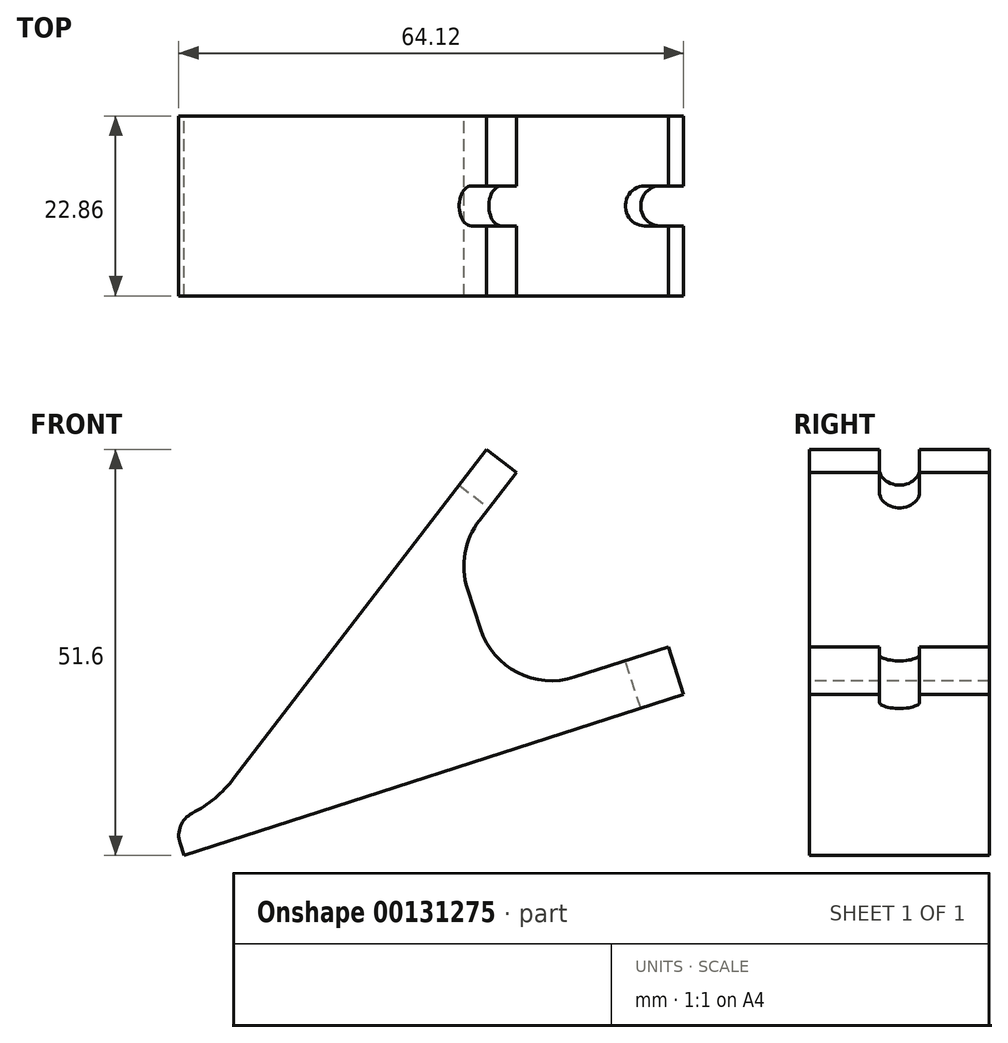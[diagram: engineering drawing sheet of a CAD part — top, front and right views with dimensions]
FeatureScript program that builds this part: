
annotation { "Feature Type Name" : "Feature", "Feature Type Description" : "" }
export const myFeature = defineFeature(function(context is Context, id is Id, definition is map)
    precondition{}
    {
        {
            var Q0;
            Q0=qCreatedBy(makeId("Front.planeOp"),FACE);
            var sketch = newSketch(context, id + "F0", { "sketchPlane" : qUnion([Q0])});
            skCircle(sketch, "E0", {"center": v(0, 0) * mm, "radius": 15.88 * mm});
            skLineSegment(sketch, "E1.bottom", {"start": v(61.91, 54.58) * mm, "end": v(-61.91, 54.58) * mm, "construction": true});
            skLineSegment(sketch, "E1.top", {"start": v(61.91, 187.86) * mm, "end": v(-61.91, 187.86) * mm});
            skLineSegment(sketch, "E1.left", {"start": v(61.91, 54.58) * mm, "end": v(61.91, 187.86) * mm});
            skLineSegment(sketch, "E1.right", {"start": v(-61.91, 54.58) * mm, "end": v(-61.91, 187.86) * mm});
            skPoint(sketch, "E1.middle", {"position": v(0, 121.22) * mm});
            skArc(sketch, "E2", {"start": v(61.91, 54.58) * mm, "mid": v(0, 22.8) * mm, "end": v(-61.91, 54.58) * mm});
            skLineSegment(sketch, "E3", {"start": v(-60.42, 52.58) * mm, "end": v(-12.59, -9.67) * mm});
            skLineSegment(sketch, "E4", {"start": v(60.42, 52.58) * mm, "end": v(12.59, -9.67) * mm});
            skLineSegment(sketch, "E5", {"start": v(-60.21, -40.88) * mm, "end": v(72.75, 1.96) * mm});
            skPoint(sketch, "E6", {"position": v(6.27, -19.46) * mm});
            skLineSegment(sketch, "E7", {"start": v(0, 0) * mm, "end": v(6.27, -19.46) * mm, "construction": true});
            skLineSegment(sketch, "E8", {"start": v(44.72, 32.14) * mm, "end": v(48.5, 29.24) * mm});
            skLineSegment(sketch, "E9", {"start": v(48.5, 29.24) * mm, "end": v(40.75, 19.17) * mm});
            skLineSegment(sketch, "E10", {"start": v(69.73, 0.99) * mm, "end": v(67.79, 7.03) * mm});
            skLineSegment(sketch, "E11", {"start": v(67.79, 7.03) * mm, "end": v(46.84, 0.28) * mm});
            skLineSegment(sketch, "E12", {"start": v(46.84, 0.28) * mm, "end": v(40.75, 19.17) * mm});
            skLineSegment(sketch, "E13", {"start": v(4.87, -15.1) * mm, "end": v(6.27, -19.46) * mm});
            skSolve(sketch);
        }
        {
            var Q0;
            {var subQ0=sQuery(id+"F0.wireOp",EDGE,"E8");Q0=makeQuery(id+"F0.imprint","IMPRINT",FACE,{"disambiguationData":[TD([[makeQuery(id+"F0.imprint","IMPRINT",EDGE,{"derivedFrom":subQ0}),-1.0]])]});}
            extrude(context, id + "F1", {"entities" : qUnion([Q0]), "depth" : 11.43 * mm, "hasSecondDirection" : true, "secondDirectionOppositeDirection" : true, "secondDirectionDepth" : 11.43 * mm});
        }
        {
            var Q0;
            Q0=makeQuery(id+"F1.opExtrude","SWEPT_FACE",FACE,{"disambiguationData":[OSD([sQuery(id+"F0.wireOp",EDGE,"E11")])]});
            var sketch = newSketch(context, id + "F2", { "sketchPlane" : qUnion([Q0])});
            skCircle(sketch, "E14", {"center": v(63.5, 0) * mm, "radius": 2.54 * mm});
            skLineSegment(sketch, "E15", {"start": v(63.5, 2.54) * mm, "end": v(66.68, 2.54) * mm});
            skLineSegment(sketch, "E16", {"start": v(63.5, -2.54) * mm, "end": v(66.68, -2.54) * mm});
            skSolve(sketch);
        }
        {
            var Q0;
            Q0=makeQuery(id+"F1.opExtrude","SWEPT_FACE",FACE,{"disambiguationData":[OSD([sQuery(id+"F0.wireOp",EDGE,"E9")])]});
            var sketch = newSketch(context, id + "F3", { "sketchPlane" : qUnion([Q0])});
            skCircle(sketch, "E17", {"center": v(0, 49.55) * mm, "radius": 2.54 * mm});
            skLineSegment(sketch, "E18", {"start": v(2.54, 49.55) * mm, "end": v(2.54, 52.73) * mm});
            skLineSegment(sketch, "E19", {"start": v(-2.54, 49.55) * mm, "end": v(-2.54, 52.73) * mm});
            skSolve(sketch);
        }
        {
            var Q0;
            {var subQ0=sQuery(id+"F3.wireOp",EDGE,"E17");var subQ1=makeQuery(id+"F3.imprint","INTERSECT",VERTEX,{"derivedFrom":[subQ0,sQuery(id+"F3.wireOp",EDGE,"E18")]});Q0=makeQuery(id+"F3.imprint","IMPRINT",FACE,{"disambiguationData":[TD([[makeQuery(id+"F3.imprint","IMPRINT",EDGE,{"disambiguationData":[TD([[subQ1,-1.0]])],"derivedFrom":subQ0}),1.0]])]});}
            var Q1;
            {var subQ0=sQuery(id+"F3.wireOp",EDGE,"E18");Q1=makeQuery(id+"F3.imprint","IMPRINT",FACE,{"disambiguationData":[TD([[makeQuery(id+"F3.imprint","IMPRINT",EDGE,{"derivedFrom":subQ0}),1.0]])]});}
            extrude(context, id + "F4", {"entities" : qUnion([Q0, Q1]), "operationType" : NewBodyOperationType.REMOVE, "oppositeDirection" : true, "depth" : 25.4 * mm});
        }
        {
            var Q0;
            {var subQ0=sQuery(id+"F2.wireOp",EDGE,"E14");var subQ1=makeQuery(id+"F2.imprint","INTERSECT",VERTEX,{"derivedFrom":[subQ0,sQuery(id+"F2.wireOp",EDGE,"E15")]});Q0=makeQuery(id+"F2.imprint","IMPRINT",FACE,{"disambiguationData":[TD([[makeQuery(id+"F2.imprint","IMPRINT",EDGE,{"disambiguationData":[TD([[subQ1,-1.0]])],"derivedFrom":subQ0}),1.0]])]});}
            var Q1;
            {var subQ0=sQuery(id+"F2.wireOp",EDGE,"E15");Q1=makeQuery(id+"F2.imprint","IMPRINT",FACE,{"disambiguationData":[TD([[makeQuery(id+"F2.imprint","IMPRINT",EDGE,{"derivedFrom":subQ0}),-1.0]])]});}
            extrude(context, id + "F5", {"entities" : qUnion([Q0, Q1]), "operationType" : NewBodyOperationType.REMOVE, "oppositeDirection" : true, "depth" : 25.4 * mm});
        }
        {
            var Q0;
            Q0=makeQuery(id+"F1.opExtrude","SWEPT_EDGE",EDGE,{"disambiguationData":[OSD([sQuery(id+"F0.wireOp",EDGE,"E11"),sQuery(id+"F0.wireOp",EDGE,"E12")])]});
            var Q1;
            Q1=makeQuery(id+"F1.opExtrude","SWEPT_EDGE",EDGE,{"disambiguationData":[OSD([sQuery(id+"F0.wireOp",EDGE,"E9"),sQuery(id+"F0.wireOp",EDGE,"E12")])]});
            fillet(context, id + "F6", {"entities" : qUnion([Q0, Q1]), "radius" : 9.52 * mm, "tangentPropagation" : true, "allowEdgeOverflow" : false});
        }
        {
            var Q0;
            Q0=makeQuery(id+"F1.opExtrude","SWEPT_EDGE",EDGE,{"disambiguationData":[OSD([sQuery(id+"F0.wireOp",EDGE,"E0"),sQuery(id+"F0.wireOp",EDGE,"E13")])]});
            fillet(context, id + "F7", {"entities" : qUnion([Q0]), "radius" : 3.17 * mm, "tangentPropagation" : true, "allowEdgeOverflow" : false});
        }
    });
